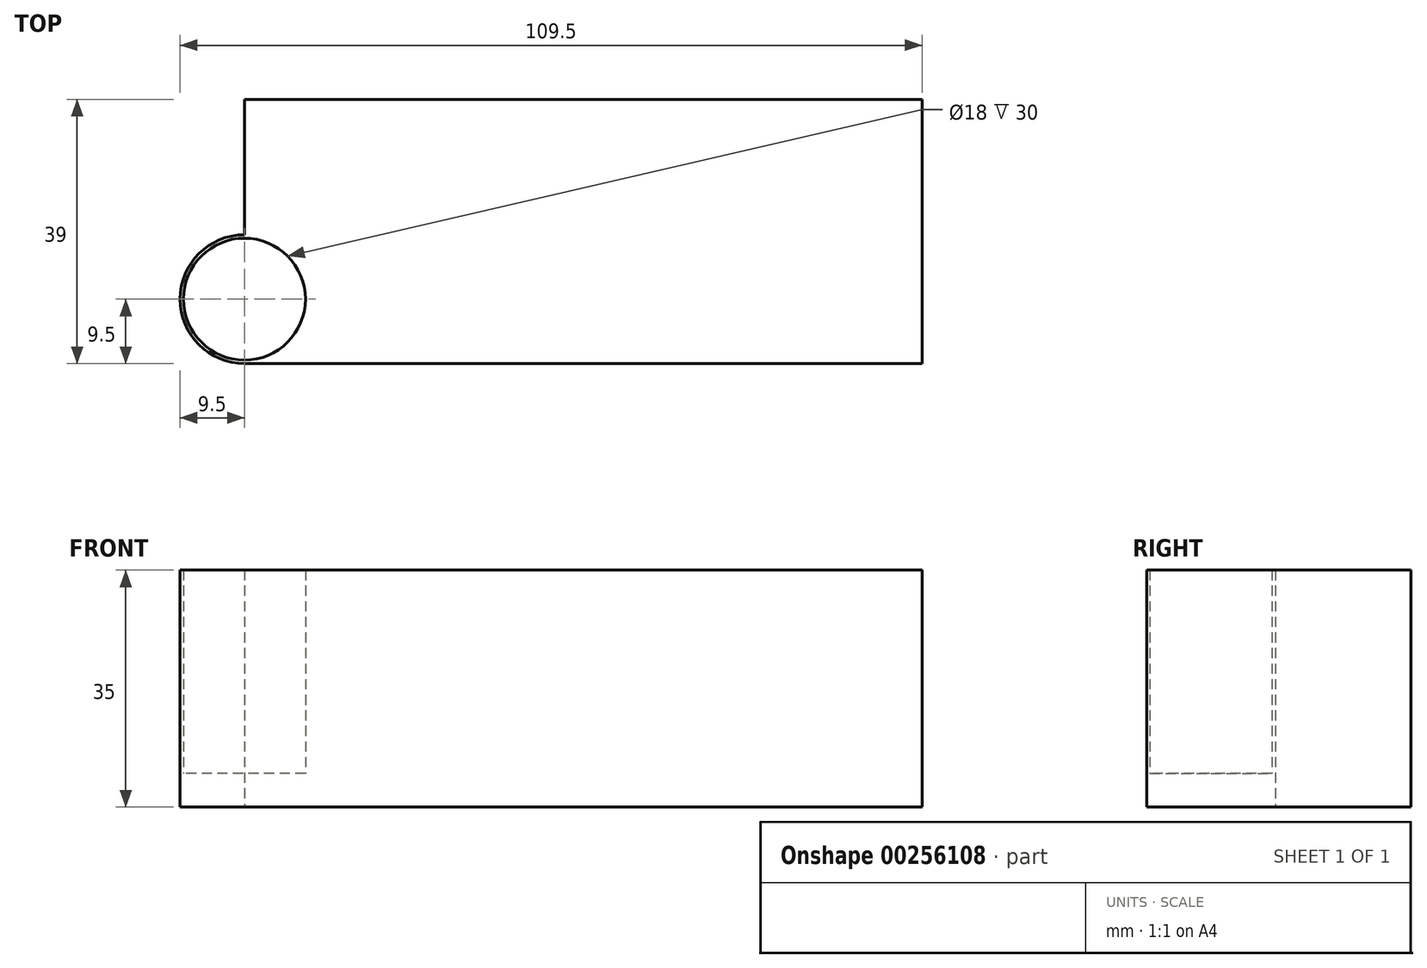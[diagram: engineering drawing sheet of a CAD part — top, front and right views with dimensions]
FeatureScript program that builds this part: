
annotation { "Feature Type Name" : "Feature", "Feature Type Description" : "" }
export const myFeature = defineFeature(function(context is Context, id is Id, definition is map)
    precondition{}
    {
        {
            var Q0;
            Q0=qCreatedBy(makeId("Top.planeOp"),FACE);
            var sketch = newSketch(context, id + "F0", { "sketchPlane" : qUnion([Q0])});
            skCircle(sketch, "E0", {"center": v(0, 0) * mm, "radius": 9 * mm});
            skCircle(sketch, "E1", {"center": v(0, 0) * mm, "radius": 9.5 * mm});
            skLineSegment(sketch, "E2", {"start": v(0, 0) * mm, "end": v(0, -9.5) * mm});
            skLineSegment(sketch, "E3", {"start": v(0, -9.5) * mm, "end": v(100, -9.5) * mm});
            skLineSegment(sketch, "E4", {"start": v(0, 0) * mm, "end": v(0, 9.5) * mm});
            skLineSegment(sketch, "E5", {"start": v(0, 9.5) * mm, "end": v(100, 9.5) * mm});
            skLineSegment(sketch, "E6", {"start": v(100, 9.5) * mm, "end": v(100, -9.5) * mm});
            skSolve(sketch);
        }
        {
            var Q0;
            Q0 = qSketchRegion(id + "F0", true);
            extrude(context, id + "F1", {"entities" : qUnion([Q0]), "depth" : 30 * mm});
        }
        {
            var Q0;
            {var subQ0=sQuery(id+"F0.wireOp",EDGE,"E3");Q0=makeQuery(id+"F0.imprint","IMPRINT",FACE,{"disambiguationData":[TD([[makeQuery(id+"F0.imprint","IMPRINT",EDGE,{"derivedFrom":subQ0}),1.0]])]});}
            var Q1;
            {var subQ0=sQuery(id+"F0.wireOp",EDGE,"E2");var subQ1=sQuery(id+"F0.wireOp",EDGE,"E0");var subQ2=makeQuery(id+"F0.imprint","INTERSECT",VERTEX,{"derivedFrom":[subQ1,subQ0]});Q1=makeQuery(id+"F0.imprint","IMPRINT",FACE,{"disambiguationData":[TD([[makeQuery(id+"F0.imprint","IMPRINT",EDGE,{"disambiguationData":[TD([[subQ2,-1.0]])],"derivedFrom":subQ1}),-1.0]])]});}
            var Q2;
            {var subQ0=sQuery(id+"F0.wireOp",EDGE,"E2");var subQ1=sQuery(id+"F0.wireOp",EDGE,"E0");var subQ2=makeQuery(id+"F0.imprint","INTERSECT",VERTEX,{"derivedFrom":[subQ1,subQ0]});Q2=makeQuery(id+"F0.imprint","IMPRINT",FACE,{"disambiguationData":[TD([[makeQuery(id+"F0.imprint","IMPRINT",EDGE,{"disambiguationData":[TD([[subQ2,-1.0]])],"derivedFrom":subQ1}),1.0]])]});}
            var Q3;
            {var subQ0=sQuery(id+"F0.wireOp",EDGE,"E2");var subQ1=sQuery(id+"F0.wireOp",EDGE,"E0");var subQ2=makeQuery(id+"F0.imprint","INTERSECT",VERTEX,{"derivedFrom":[subQ1,subQ0]});Q3=makeQuery(id+"F0.imprint","IMPRINT",FACE,{"disambiguationData":[TD([[makeQuery(id+"F0.imprint","IMPRINT",EDGE,{"disambiguationData":[TD([[subQ2,1.0]])],"derivedFrom":subQ1}),-1.0]])]});}
            var Q4;
            {var subQ0=sQuery(id+"F0.wireOp",EDGE,"E2");var subQ1=sQuery(id+"F0.wireOp",EDGE,"E0");var subQ2=makeQuery(id+"F0.imprint","INTERSECT",VERTEX,{"derivedFrom":[subQ1,subQ0]});Q4=makeQuery(id+"F0.imprint","IMPRINT",FACE,{"disambiguationData":[TD([[makeQuery(id+"F0.imprint","IMPRINT",EDGE,{"disambiguationData":[TD([[subQ2,1.0]])],"derivedFrom":subQ1}),1.0]])]});}
            extrude(context, id + "F2", {"entities" : qUnion([Q0, Q1, Q2, Q3, Q4]), "operationType" : NewBodyOperationType.ADD, "oppositeDirection" : true, "depth" : 20 * mm});
        }
        {
            var Q0;
            {var subQ0=sQuery(id+"F0.wireOp",EDGE,"E5");Q0=makeQuery(id+"F2.boolean.opBoolean","MERGE",FACE,{"derivedFrom":[makeQuery(id+"F1.opExtrude","SWEPT_FACE",FACE,{"disambiguationData":[OSD([subQ0])]}),makeQuery(id+"F2.opExtrude","SWEPT_FACE",FACE,{"disambiguationData":[OSD([subQ0])]})]});}
            extrude(context, id + "F3", {"entities" : qUnion([Q0]), "operationType" : NewBodyOperationType.ADD, "depth" : 20 * mm});
        }
        {
            var Q0;
            {var subQ0=sQuery(id+"F0.wireOp",EDGE,"E5");Q0=makeQuery(id+"F3.boolean.opBoolean","MERGE",FACE,{"derivedFrom":[makeQuery(id+"F2.opExtrude","CAP_FACE",FACE,{"disambiguationData":[OSD([sQuery(id+"F0.wireOp",EDGE,"E1"),sQuery(id+"F0.wireOp",EDGE,"E3"),subQ0,sQuery(id+"F0.wireOp",EDGE,"E6")])],"isStart":false}),makeQuery(id+"F3.opExtrude","SWEPT_FACE",FACE,{"disambiguationData":[OSD([subQ0]),TDD([makeQuery(id+"F2.opExtrude","CAP_EDGE",EDGE,{"disambiguationData":[OSD([subQ0])],"isStart":false})])]})]});}
            extrude(context, id + "F4", {"entities" : qUnion([Q0]), "operationType" : NewBodyOperationType.REMOVE, "oppositeDirection" : true, "depth" : 15 * mm});
        }
    });
